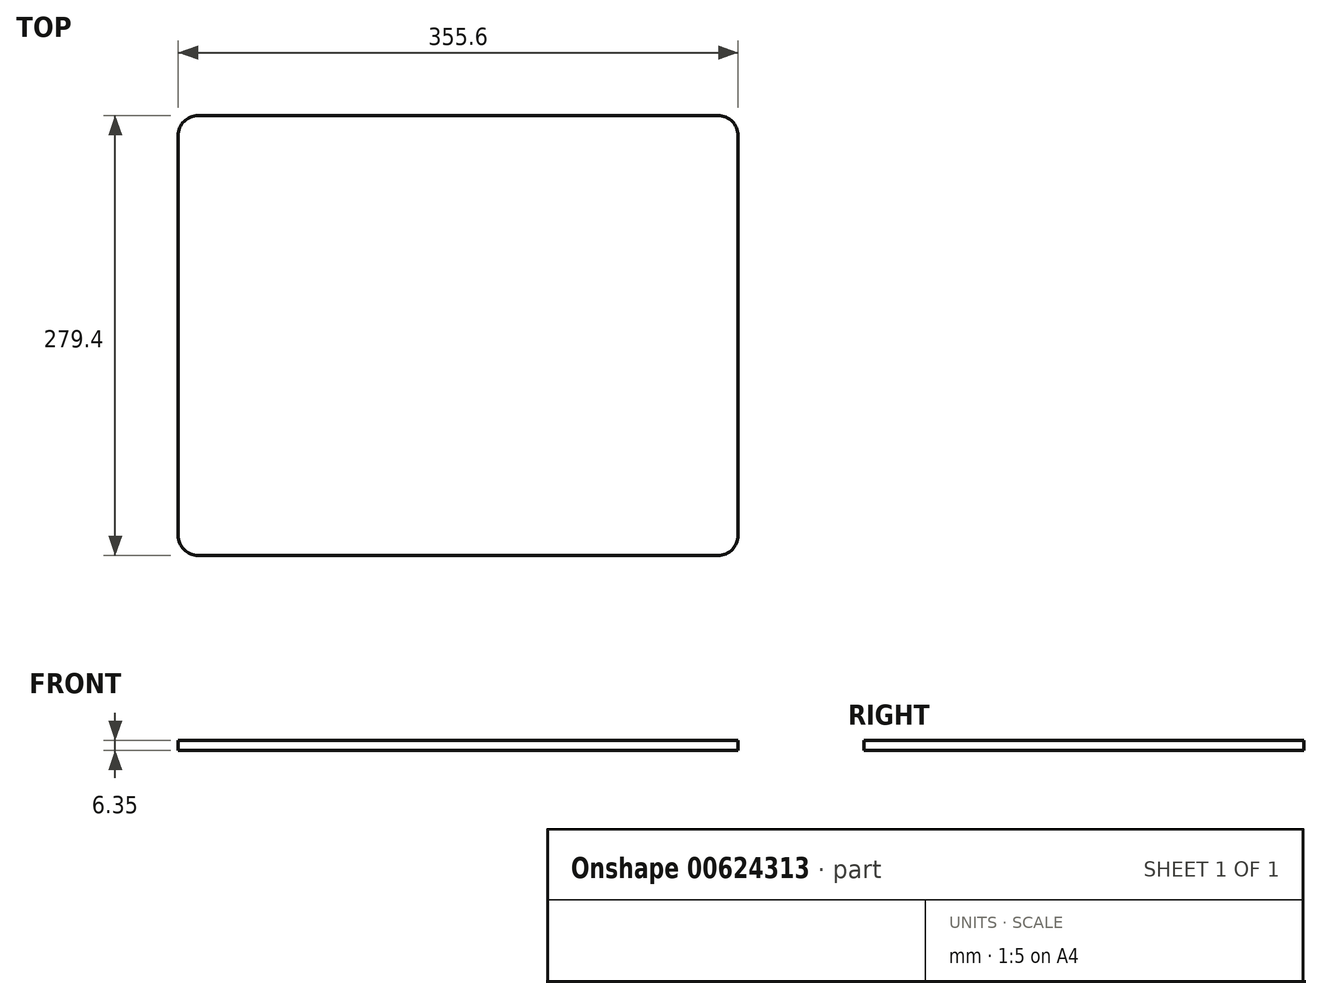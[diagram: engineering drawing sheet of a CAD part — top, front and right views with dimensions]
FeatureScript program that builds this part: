
annotation { "Feature Type Name" : "Feature", "Feature Type Description" : "" }
export const myFeature = defineFeature(function(context is Context, id is Id, definition is map)
    precondition{}
    {
        {
            var Q0;
            Q0=qCreatedBy(makeId("Top.planeOp"),FACE);
            var sketch = newSketch(context, id + "F0", { "sketchPlane" : qUnion([Q0])});
            skLineSegment(sketch, "E0.bottom", {"start": v(177.8, -139.7) * mm, "end": v(-177.8, -139.7) * mm});
            skLineSegment(sketch, "E0.top", {"start": v(177.8, 139.7) * mm, "end": v(-177.8, 139.7) * mm});
            skLineSegment(sketch, "E0.left", {"start": v(177.8, -139.7) * mm, "end": v(177.8, 139.7) * mm});
            skLineSegment(sketch, "E0.right", {"start": v(-177.8, -139.7) * mm, "end": v(-177.8, 139.7) * mm});
            skPoint(sketch, "E0.middle", {"position": v(0, 0) * mm});
            skSolve(sketch);
        }
        {
            var Q0;
            Q0 = qSketchRegion(id + "F0", true);
            extrude(context, id + "F1", {"entities" : qUnion([Q0]), "depth" : 6.35 * mm, "offsetDistance" : 25.4 * mm});
        }
        {
            var Q0;
            Q0=makeQuery(id+"F1.opExtrude","SWEPT_EDGE",EDGE,{"disambiguationData":[OSD([sQuery(id+"F0.wireOp",EDGE,"E0.bottom"),sQuery(id+"F0.wireOp",EDGE,"E0.right")])]});
            var Q1;
            Q1=makeQuery(id+"F1.opExtrude","SWEPT_EDGE",EDGE,{"disambiguationData":[OSD([sQuery(id+"F0.wireOp",EDGE,"E0.bottom"),sQuery(id+"F0.wireOp",EDGE,"E0.left")])]});
            var Q2;
            Q2=makeQuery(id+"F1.opExtrude","SWEPT_EDGE",EDGE,{"disambiguationData":[OSD([sQuery(id+"F0.wireOp",EDGE,"E0.top"),sQuery(id+"F0.wireOp",EDGE,"E0.left")])]});
            var Q3;
            Q3=makeQuery(id+"F1.opExtrude","SWEPT_EDGE",EDGE,{"disambiguationData":[OSD([sQuery(id+"F0.wireOp",EDGE,"E0.top"),sQuery(id+"F0.wireOp",EDGE,"E0.right")])]});
            fillet(context, id + "F2", {"entities" : qUnion([Q0, Q1, Q2, Q3]), "radius" : 12.7 * mm, "tangentPropagation" : true, "allowEdgeOverflow" : false});
        }
    });
